# Revit family: Haworth_ActiveComponents_WedgeFullConferenceEnd_BUILD
name_source: partatom
category: Furniture Systems
revit_build: Autodesk Revit Architecture 2015 (Build: 20141119_1515(x64)
units: mm (PartAtom-declared; Revit-internal decimal feet)

## types (8) — shared parameters
Actual Height = 29 3/16"
Angled Leg Offset = 5 3/4"
Assembly Code = E2020200
Description = Haworth - Active Components - Wedge Full Conference End
Inside Radius = 1 1/2"
Manufacturer = Haworth
Max. Depth = 36"
Max. Width = 72"
Min. Depth = 28"
Min. Width = 60"
Model = WAYD
Radius = 3 1/2"
Revision Number = 1
Size = Verify Final Dim. w/ Haworth
Thickness = 1 3/16"
URL = www.haworth.com
URL - Product = https://www.haworth.com
Warranty = https://www.haworth.com
With Leg = Yes

## per-type parameters (varying)
| type | Actual Depth | Actual Width | Angled Leg Control | Column Leg Control | Column Leg Offset | Depth | Overall Depth | Overhang | Panel Width | Surface Angle | Width |
| 36d 72w - 66 Panel Width | 36" | 72" | Yes | No | 8 15/16" | 36" | 39" | 6" | 66" | 9.00° | 72" |
| 30d 72w - 66 Panel Width | 30" | 72" | Yes | No | 8 15/16" | 30" | 33" | 6" | 66" | 7.00° | 72" |
| 28d 60w - 54 Panel Width | 28" | 60" | Yes | No | 7 15/16" | 28" | 31" | 6" | 54" | 7.00° | 60" |
| 34d 60w - 54 Panel Width | 34" | 60" | Yes | No | 7 15/16" | 34" | 37" | 6" | 54" | 9.00° | 60" |
| 36d 72w - 48 Panel Width | 36" | 72" | No | Yes | 8 15/16" | 36" | 39" | 24" | 48" | 9.00° | 72" |
| 34d 60w - 42 Panel Width | 34" | 60" | No | Yes | 7 15/16" | 34" | 37" | 18" | 42" | 9.00° | 60" |
| 30d 72w - 48 Panel Width | 30" | 72" | No | Yes | 8 15/16" | 30" | 33" | 24" | 48" | 7.00° | 72" |
| 28d 60w - 42 Panel Width | 28" | 60" | No | Yes | 7 15/16" | 28" | 31" | 18" | 42" | 7.00° | 60" |

## geometry (parser evidence)
native form markers: Blend x49, Sweep x8
no freeform markers — native parametric forms only
